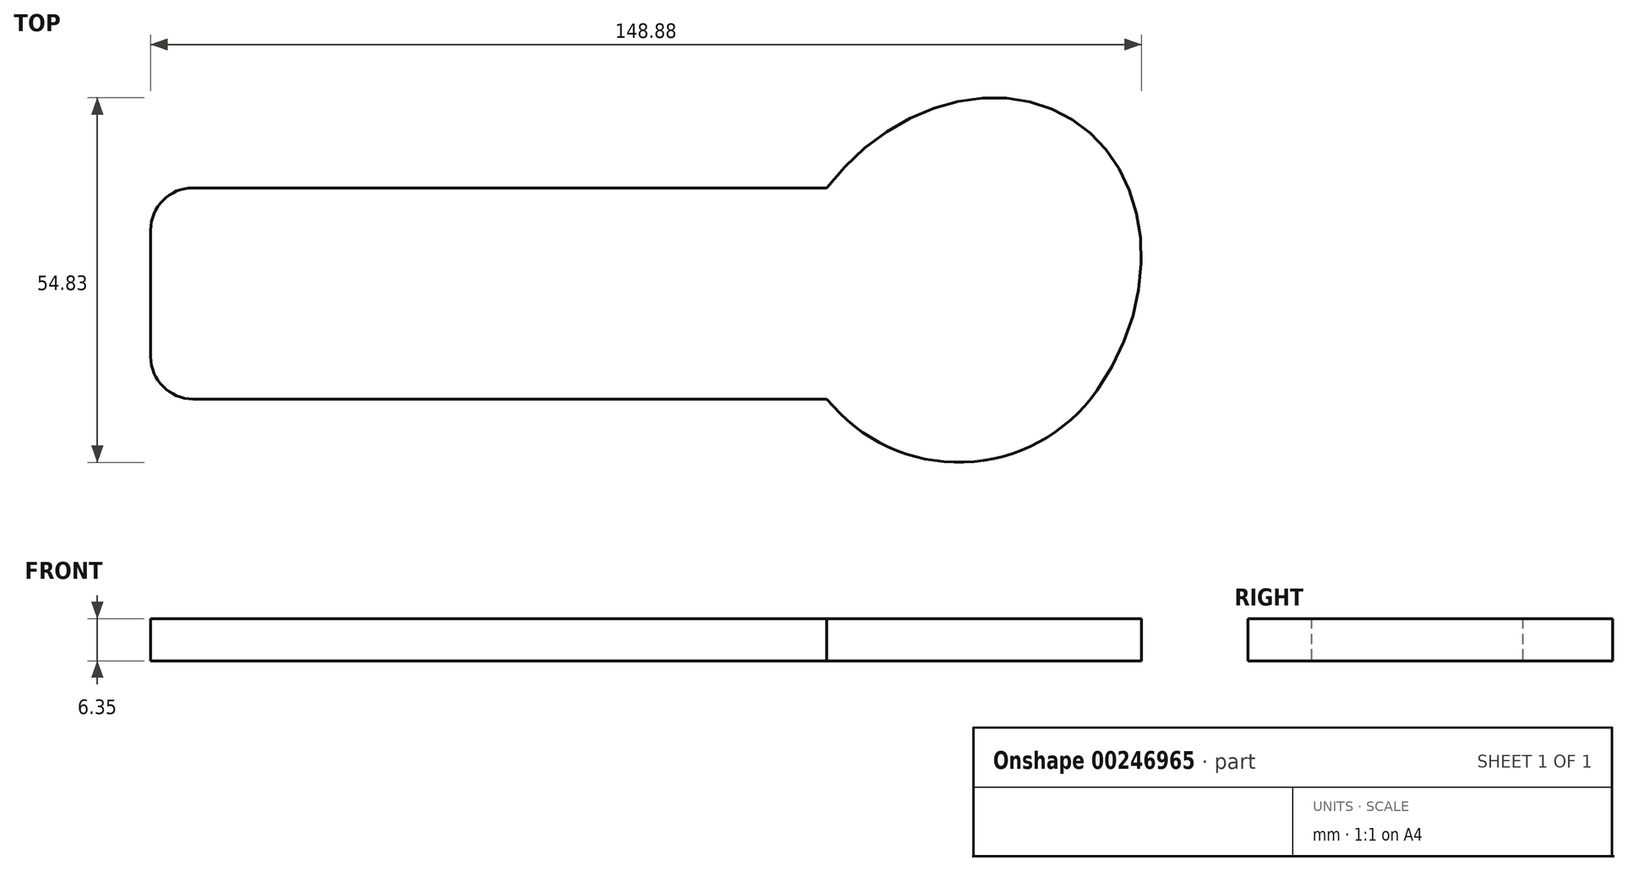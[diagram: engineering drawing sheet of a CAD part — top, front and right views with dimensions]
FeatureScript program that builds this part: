
annotation { "Feature Type Name" : "Feature", "Feature Type Description" : "" }
export const myFeature = defineFeature(function(context is Context, id is Id, definition is map)
    precondition{}
    {
        {
            var Q0;
            Q0=qCreatedBy(makeId("Top.planeOp"),FACE);
            var sketch = newSketch(context, id + "F0", { "sketchPlane" : qUnion([Q0])});
            skLineSegment(sketch, "E0", {"start": v(0, 38.1) * mm, "end": v(35.8, 13.03) * mm});
            skLineSegment(sketch, "E1", {"start": v(0, 0) * mm, "end": v(58.42, 0) * mm});
            skArc(sketch, "E2", {"start": v(-20.8, 14.57) * mm, "mid": v(-14.57, -20.8) * mm, "end": v(20.8, -14.57) * mm});
            skEllipticalArc(sketch, "E3", {});
            skPoint(sketch, "E4", {"position": v(17.9, 25.57) * mm});
            skLineSegment(sketch, "E5", {"start": v(-19.83, -15.87) * mm, "end": v(-121.43, -15.88) * mm});
            skLineSegment(sketch, "E6", {"start": v(-121.43, -15.87) * mm, "end": v(-121.43, 15.88) * mm});
            skLineSegment(sketch, "E7", {"start": v(-121.43, 15.88) * mm, "end": v(-19.83, 15.88) * mm});
            skPoint(sketch, "E8", {"position": v(-121.43, 0) * mm});
            const initialGuessF0  = {"E3": [0, 0, 0.573576436351046, 0.8191520442889919, 0.031209692887410587, 0.0254, 4.71238898038469, 1.5707963267948966]};
            skSetInitialGuess(sketch, initialGuessF0);
            skSolve(sketch);
        }
        {
            var Q0;
            Q0 = qSketchRegion(id + "F0", true);
            extrude(context, id + "F1", {"entities" : qUnion([Q0]), "depth" : 6.35 * mm});
        }
        {
            var Q0;
            Q0=makeQuery(id+"F1.opExtrude","SWEPT_EDGE",EDGE,{"disambiguationData":[OSD([sQuery(id+"F0.wireOp",EDGE,"E6"),sQuery(id+"F0.wireOp",EDGE,"E7")])]});
            var Q1;
            Q1=makeQuery(id+"F1.opExtrude","SWEPT_EDGE",EDGE,{"disambiguationData":[OSD([sQuery(id+"F0.wireOp",EDGE,"E5"),sQuery(id+"F0.wireOp",EDGE,"E6")])]});
            fillet(context, id + "F2", {"entities" : qUnion([Q0, Q1]), "radius" : 6.35 * mm, "tangentPropagation" : true, "allowEdgeOverflow" : false});
        }
    });
